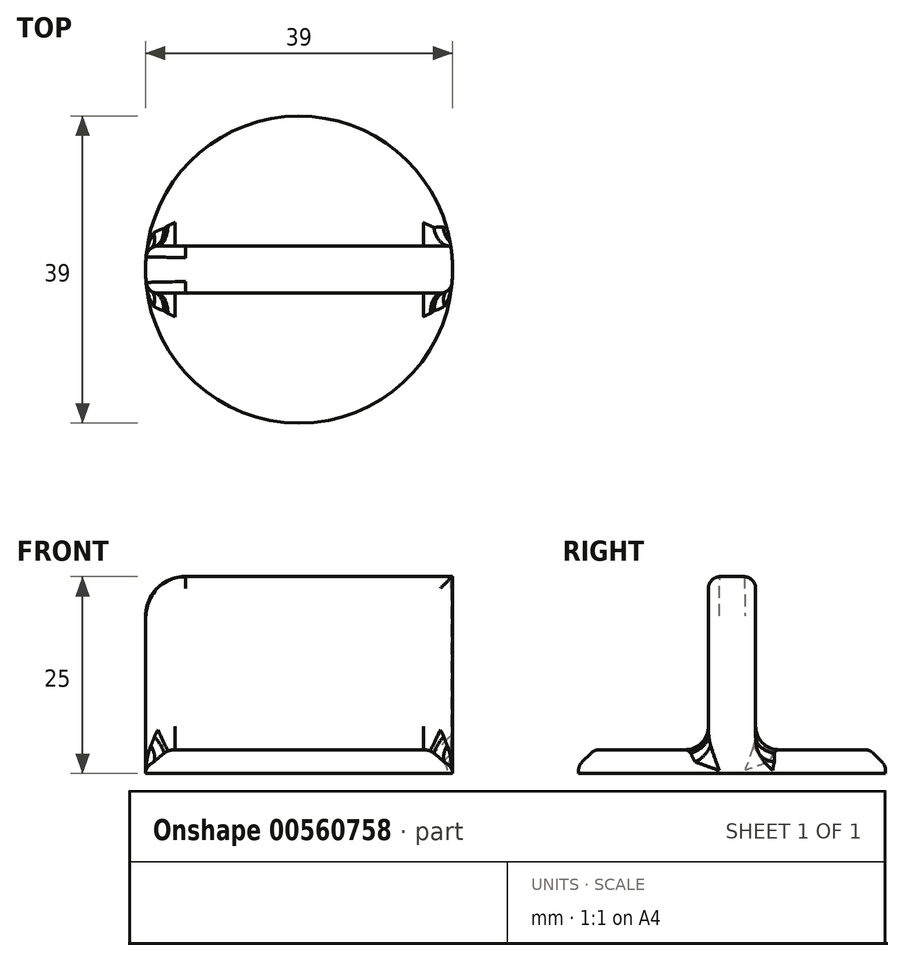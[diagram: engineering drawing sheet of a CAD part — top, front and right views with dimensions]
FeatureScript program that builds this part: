
annotation { "Feature Type Name" : "Feature", "Feature Type Description" : "" }
export const myFeature = defineFeature(function(context is Context, id is Id, definition is map)
    precondition{}
    {
        {
            var Q0;
            Q0=qCreatedBy(makeId("Top.planeOp"),FACE);
            var sketch = newSketch(context, id + "F0", { "sketchPlane" : qUnion([Q0])});
            skCircle(sketch, "E0", {"center": v(0, 0) * mm, "radius": 19.5 * mm});
            skLineSegment(sketch, "E1", {"start": v(0, 0) * mm, "end": v(19.5, 0) * mm});
            skLineSegment(sketch, "E2", {"start": v(19.5, 0) * mm, "end": v(-19.5, 0) * mm});
            skLineSegment(sketch, "E3.0", {"start": v(19.27, 3) * mm, "end": v(-19.27, 3) * mm});
            skLineSegment(sketch, "E4.0", {"start": v(19.27, -3) * mm, "end": v(-19.27, -3) * mm});
            skSolve(sketch);
        }
        {
            var Q0;
            Q0 = qSketchRegion(id + "F0", true);
            extrude(context, id + "F1", {"entities" : qUnion([Q0]), "depth" : 3 * mm, "offsetDistance" : 25 * mm});
        }
        {
            var Q0;
            {var subQ5=sQuery(id+"F0.wireOp",EDGE,"E4.0");Q0=makeQuery(id+"F0.imprint","IMPRINT",FACE,{"disambiguationData":[TD([[makeQuery(id+"F0.imprint","IMPRINT",EDGE,{"derivedFrom":subQ5}),-1.0]])]});}
            var Q1;
            {var subQ5=sQuery(id+"F0.wireOp",EDGE,"E3.0");Q1=makeQuery(id+"F0.imprint","IMPRINT",FACE,{"disambiguationData":[TD([[makeQuery(id+"F0.imprint","IMPRINT",EDGE,{"derivedFrom":subQ5}),1.0]])]});}
            extrude(context, id + "F2", {"entities" : qUnion([Q0, Q1]), "operationType" : NewBodyOperationType.ADD, "depth" : 25 * mm, "offsetDistance" : 25 * mm});
        }
        {
            var Q0;
            {var subQ0=sQuery(id+"F0.wireOp",EDGE,"E0");var subQ1=makeQuery(id+"F0.imprint","INTERSECT",VERTEX,{"disambiguationData":[OD(1.0)],"derivedFrom":[subQ0,sQuery(id+"F0.wireOp",EDGE,"E2")]});Q0=makeQuery(id+"F2.opExtrude","CAP_EDGE",EDGE,{"disambiguationData":[OSD([subQ0]),TDD([makeQuery(id+"F0.imprint","IMPRINT",EDGE,{"disambiguationData":[TD([[subQ1,1.0]])],"derivedFrom":subQ0}),makeQuery(id+"F0.imprint","IMPRINT",EDGE,{"disambiguationData":[TD([[subQ1,-1.0]])],"derivedFrom":subQ0})])],"isStart":false});}
            var Q1;
            {var subQ0=sQuery(id+"F0.wireOp",EDGE,"E0");var subQ1=makeQuery(id+"F0.imprint","INTERSECT",VERTEX,{"disambiguationData":[OD(0.0)],"derivedFrom":[subQ0,sQuery(id+"F0.wireOp",EDGE,"E2")]});Q1=makeQuery(id+"F2.opExtrude","CAP_EDGE",EDGE,{"disambiguationData":[OSD([subQ0]),TDD([makeQuery(id+"F0.imprint","IMPRINT",EDGE,{"disambiguationData":[TD([[subQ1,-1.0]])],"derivedFrom":subQ0}),makeQuery(id+"F0.imprint","IMPRINT",EDGE,{"disambiguationData":[TD([[subQ1,1.0]])],"derivedFrom":subQ0})])],"isStart":false});}
            fillet(context, id + "F3", {"entities" : qUnion([Q0, Q1]), "radius" : 5 * mm, "tangentPropagation" : true, "allowEdgeOverflow" : false});
        }
        {
            var Q0;
            {var subQ1=sQuery(id+"F0.wireOp",EDGE,"E0");var subQ3=sQuery(id+"F0.wireOp",EDGE,"E4.0");Q0=makeQuery(id+"F2.boolean.opBoolean","SPLIT",EDGE,{"disambiguationData":[TD([makeQuery(id+"F2.opExtrude","SWEPT_FACE",FACE,{"disambiguationData":[OSD([subQ3])]})])],"derivedFrom":makeQuery(id+"F1.opExtrude","CAP_EDGE",EDGE,{"disambiguationData":[OSD([subQ1])],"isStart":false})});}
            var Q1;
            {var subQ1=sQuery(id+"F0.wireOp",EDGE,"E0");var subQ4=sQuery(id+"F0.wireOp",EDGE,"E3.0");Q1=makeQuery(id+"F2.boolean.opBoolean","SPLIT",EDGE,{"disambiguationData":[TD([makeQuery(id+"F2.opExtrude","SWEPT_FACE",FACE,{"disambiguationData":[OSD([subQ4])]})])],"derivedFrom":makeQuery(id+"F1.opExtrude","CAP_EDGE",EDGE,{"disambiguationData":[OSD([subQ1])],"isStart":false})});}
            chamfer(context, id + "F4", {"entities" : qUnion([Q0, Q1]), "width" : 2 * mm, "tangentPropagation" : true});
        }
        {
            var Q0;
            {var subQ0=sQuery(id+"F0.wireOp",EDGE,"E4.0");var subQ1=sQuery(id+"F0.wireOp",EDGE,"E0");var subQ2=makeQuery(id+"F0.imprint","INTERSECT",VERTEX,{"disambiguationData":[OD(1.0)],"derivedFrom":[subQ1,sQuery(id+"F0.wireOp",EDGE,"E2")]});Q0=makeQuery(id+"F3.opFillet","BLEND_EDGE",EDGE,{"blendedFrom":[makeQuery(id+"F2.opExtrude","CAP_EDGE",EDGE,{"disambiguationData":[OSD([subQ1]),TDD([makeQuery(id+"F0.imprint","IMPRINT",EDGE,{"disambiguationData":[TD([[subQ2,1.0]])],"derivedFrom":subQ1}),makeQuery(id+"F0.imprint","IMPRINT",EDGE,{"disambiguationData":[TD([[subQ2,-1.0]])],"derivedFrom":subQ1})])],"isStart":false}),makeQuery(id+"F2.opExtrude","SWEPT_FACE",FACE,{"disambiguationData":[OSD([subQ0])]})],"blendedInto":[makeQuery(id+"F2.opExtrude","SWEPT_FACE",FACE,{"disambiguationData":[OSD([subQ0])]})]});}
            var Q1;
            Q1=makeQuery(id+"F2.opExtrude","CAP_EDGE",EDGE,{"disambiguationData":[OSD([sQuery(id+"F0.wireOp",EDGE,"E4.0")])],"isStart":false});
            var Q2;
            {var subQ0=sQuery(id+"F0.wireOp",EDGE,"E4.0");var subQ1=sQuery(id+"F0.wireOp",EDGE,"E0");var subQ2=makeQuery(id+"F0.imprint","INTERSECT",VERTEX,{"disambiguationData":[OD(0.0)],"derivedFrom":[subQ1,sQuery(id+"F0.wireOp",EDGE,"E2")]});Q2=makeQuery(id+"F3.opFillet","BLEND_EDGE",EDGE,{"blendedFrom":[makeQuery(id+"F2.opExtrude","CAP_EDGE",EDGE,{"disambiguationData":[OSD([subQ1]),TDD([makeQuery(id+"F0.imprint","IMPRINT",EDGE,{"disambiguationData":[TD([[subQ2,-1.0]])],"derivedFrom":subQ1}),makeQuery(id+"F0.imprint","IMPRINT",EDGE,{"disambiguationData":[TD([[subQ2,1.0]])],"derivedFrom":subQ1})])],"isStart":false}),makeQuery(id+"F2.opExtrude","SWEPT_FACE",FACE,{"disambiguationData":[OSD([subQ0])]})],"blendedInto":[makeQuery(id+"F2.opExtrude","SWEPT_FACE",FACE,{"disambiguationData":[OSD([subQ0])]})]});}
            var Q3;
            {var subQ0=sQuery(id+"F0.wireOp",EDGE,"E4.0");var subQ1=sQuery(id+"F0.wireOp",EDGE,"E0");Q3=makeQuery(id+"F2.opExtrude","SWEPT_EDGE",EDGE,{"disambiguationData":[OSD([subQ1,subQ0]),TDD([makeQuery(id+"F0.imprint","INTERSECT",VERTEX,{"disambiguationData":[OD(0.0)],"derivedFrom":[subQ1,subQ0]})])]});}
            var Q4;
            {var subQ0=sQuery(id+"F0.wireOp",EDGE,"E4.0");var subQ1=sQuery(id+"F0.wireOp",EDGE,"E0");Q4=makeQuery(id+"F2.opExtrude","SWEPT_EDGE",EDGE,{"disambiguationData":[OSD([subQ1,subQ0]),TDD([makeQuery(id+"F0.imprint","INTERSECT",VERTEX,{"disambiguationData":[OD(1.0)],"derivedFrom":[subQ1,subQ0]})])]});}
            var Q5;
            Q5=makeQuery(id+"F2.opExtrude","CAP_EDGE",EDGE,{"disambiguationData":[OSD([sQuery(id+"F0.wireOp",EDGE,"E3.0")])],"isStart":false});
            var Q6;
            {var subQ0=sQuery(id+"F0.wireOp",EDGE,"E0");var subQ2=sQuery(id+"F0.wireOp",EDGE,"E3.0");var subQ3=makeQuery(id+"F2.opExtrude","SWEPT_FACE",FACE,{"disambiguationData":[OSD([subQ2])]});var subQ10=makeQuery(id+"F1.opExtrude","CAP_FACE",FACE,{"disambiguationData":[OSD([subQ0])],"isStart":false});Q6=makeQuery(id+"F4.opChamfer","BLEND_EDGE",EDGE,{"blendedFrom":[makeQuery(id+"F2.boolean.opBoolean","SPLIT",EDGE,{"disambiguationData":[TD([subQ3])],"derivedFrom":makeQuery(id+"F1.opExtrude","CAP_EDGE",EDGE,{"disambiguationData":[OSD([subQ0])],"isStart":false})}),makeQuery(id+"F2.boolean.opBoolean","SPLIT",FACE,{"disambiguationData":[TD([subQ3])],"derivedFrom":subQ10})],"blendedInto":[makeQuery(id+"F2.boolean.opBoolean","SPLIT",FACE,{"disambiguationData":[TD([subQ3])],"derivedFrom":subQ10})]});}
            var Q7;
            {var subQ0=sQuery(id+"F0.wireOp",EDGE,"E0");var subQ4=sQuery(id+"F0.wireOp",EDGE,"E4.0");var subQ9=makeQuery(id+"F2.opExtrude","SWEPT_FACE",FACE,{"disambiguationData":[OSD([subQ4])]});var subQ10=makeQuery(id+"F1.opExtrude","CAP_FACE",FACE,{"disambiguationData":[OSD([subQ0])],"isStart":false});Q7=makeQuery(id+"F4.opChamfer","BLEND_EDGE",EDGE,{"blendedFrom":[makeQuery(id+"F2.boolean.opBoolean","SPLIT",EDGE,{"disambiguationData":[TD([subQ9])],"derivedFrom":makeQuery(id+"F1.opExtrude","CAP_EDGE",EDGE,{"disambiguationData":[OSD([subQ0])],"isStart":false})}),makeQuery(id+"F2.boolean.opBoolean","SPLIT",FACE,{"disambiguationData":[TD([subQ9])],"derivedFrom":subQ10})],"blendedInto":[makeQuery(id+"F2.boolean.opBoolean","SPLIT",FACE,{"disambiguationData":[TD([subQ9])],"derivedFrom":subQ10})]});}
            var Q8;
            {var subQ0=sQuery(id+"F0.wireOp",EDGE,"E2");var subQ1=sQuery(id+"F0.wireOp",EDGE,"E0");var subQ2=makeQuery(id+"F0.imprint","INTERSECT",VERTEX,{"disambiguationData":[OD(1.0)],"derivedFrom":[subQ1,subQ0]});var subQ3=sQuery(id+"F0.wireOp",EDGE,"E4.0");var subQ5=makeQuery(id+"F2.opExtrude","SWEPT_FACE",FACE,{"disambiguationData":[OSD([subQ1]),TDD([makeQuery(id+"F0.imprint","IMPRINT",EDGE,{"disambiguationData":[TD([[subQ2,1.0]])],"derivedFrom":subQ1}),makeQuery(id+"F0.imprint","IMPRINT",EDGE,{"disambiguationData":[TD([[subQ2,-1.0]])],"derivedFrom":subQ1})])]});var subQ6=makeQuery(id+"F0.imprint","INTERSECT",VERTEX,{"disambiguationData":[OD(0.0)],"derivedFrom":[subQ1,subQ0]});var subQ7=makeQuery(id+"F2.opExtrude","SWEPT_FACE",FACE,{"disambiguationData":[OSD([subQ1]),TDD([makeQuery(id+"F0.imprint","IMPRINT",EDGE,{"disambiguationData":[TD([[subQ6,-1.0]])],"derivedFrom":subQ1}),makeQuery(id+"F0.imprint","IMPRINT",EDGE,{"disambiguationData":[TD([[subQ6,1.0]])],"derivedFrom":subQ1})])]});var subQ8=makeQuery(id+"F1.opExtrude","SWEPT_FACE",FACE,{"disambiguationData":[OSD([subQ1])]});Q8=makeQuery(id+"F4.opChamfer","BLEND_EDGE",EDGE,{"blendedFrom":[makeQuery(id+"F2.boolean.opBoolean","SPLIT",EDGE,{"disambiguationData":[TD([makeQuery(id+"F2.opExtrude","SWEPT_FACE",FACE,{"disambiguationData":[OSD([subQ3])]})])],"derivedFrom":makeQuery(id+"F1.opExtrude","CAP_EDGE",EDGE,{"disambiguationData":[OSD([subQ1])],"isStart":false})}),makeQuery(id+"F2.boolean.opBoolean","MERGE",FACE,{"derivedFrom":[subQ8,subQ7,subQ5]})],"blendedInto":[makeQuery(id+"F2.boolean.opBoolean","MERGE",FACE,{"derivedFrom":[subQ8,subQ7,subQ5]})]});}
            var Q9;
            {var subQ0=sQuery(id+"F0.wireOp",EDGE,"E2");var subQ1=sQuery(id+"F0.wireOp",EDGE,"E0");var subQ2=makeQuery(id+"F0.imprint","INTERSECT",VERTEX,{"disambiguationData":[OD(1.0)],"derivedFrom":[subQ1,subQ0]});var subQ4=sQuery(id+"F0.wireOp",EDGE,"E3.0");var subQ5=makeQuery(id+"F2.opExtrude","SWEPT_FACE",FACE,{"disambiguationData":[OSD([subQ1]),TDD([makeQuery(id+"F0.imprint","IMPRINT",EDGE,{"disambiguationData":[TD([[subQ2,1.0]])],"derivedFrom":subQ1}),makeQuery(id+"F0.imprint","IMPRINT",EDGE,{"disambiguationData":[TD([[subQ2,-1.0]])],"derivedFrom":subQ1})])]});var subQ6=makeQuery(id+"F0.imprint","INTERSECT",VERTEX,{"disambiguationData":[OD(0.0)],"derivedFrom":[subQ1,subQ0]});var subQ7=makeQuery(id+"F2.opExtrude","SWEPT_FACE",FACE,{"disambiguationData":[OSD([subQ1]),TDD([makeQuery(id+"F0.imprint","IMPRINT",EDGE,{"disambiguationData":[TD([[subQ6,-1.0]])],"derivedFrom":subQ1}),makeQuery(id+"F0.imprint","IMPRINT",EDGE,{"disambiguationData":[TD([[subQ6,1.0]])],"derivedFrom":subQ1})])]});var subQ8=makeQuery(id+"F1.opExtrude","SWEPT_FACE",FACE,{"disambiguationData":[OSD([subQ1])]});Q9=makeQuery(id+"F4.opChamfer","BLEND_EDGE",EDGE,{"blendedFrom":[makeQuery(id+"F2.boolean.opBoolean","SPLIT",EDGE,{"disambiguationData":[TD([makeQuery(id+"F2.opExtrude","SWEPT_FACE",FACE,{"disambiguationData":[OSD([subQ4])]})])],"derivedFrom":makeQuery(id+"F1.opExtrude","CAP_EDGE",EDGE,{"disambiguationData":[OSD([subQ1])],"isStart":false})}),makeQuery(id+"F2.boolean.opBoolean","MERGE",FACE,{"derivedFrom":[subQ8,subQ7,subQ5]})],"blendedInto":[makeQuery(id+"F2.boolean.opBoolean","MERGE",FACE,{"derivedFrom":[subQ8,subQ7,subQ5]})]});}
            fillet(context, id + "F5", {"entities" : qUnion([Q0, Q1, Q2, Q3, Q4, Q5, Q6, Q7, Q8, Q9]), "radius" : 1.5 * mm, "tangentPropagation" : true, "allowEdgeOverflow" : false});
        }
        {
            var Q0;
            Q0=makeQuery(id+"F2.boolean.opBoolean","INTERSECT",EDGE,{"derivedFrom":[makeQuery(id+"F1.opExtrude","CAP_FACE",FACE,{"disambiguationData":[OSD([sQuery(id+"F0.wireOp",EDGE,"E0")])],"isStart":false}),makeQuery(id+"F2.opExtrude","SWEPT_FACE",FACE,{"disambiguationData":[OSD([sQuery(id+"F0.wireOp",EDGE,"E4.0")])]})]});
            var Q1;
            Q1=makeQuery(id+"F2.boolean.opBoolean","INTERSECT",EDGE,{"derivedFrom":[makeQuery(id+"F1.opExtrude","CAP_FACE",FACE,{"disambiguationData":[OSD([sQuery(id+"F0.wireOp",EDGE,"E0")])],"isStart":false}),makeQuery(id+"F2.opExtrude","SWEPT_FACE",FACE,{"disambiguationData":[OSD([sQuery(id+"F0.wireOp",EDGE,"E3.0")])]})]});
            fillet(context, id + "F6", {"entities" : qUnion([Q0, Q1]), "radius" : 3 * mm, "tangentPropagation" : true, "allowEdgeOverflow" : false});
        }
    });
